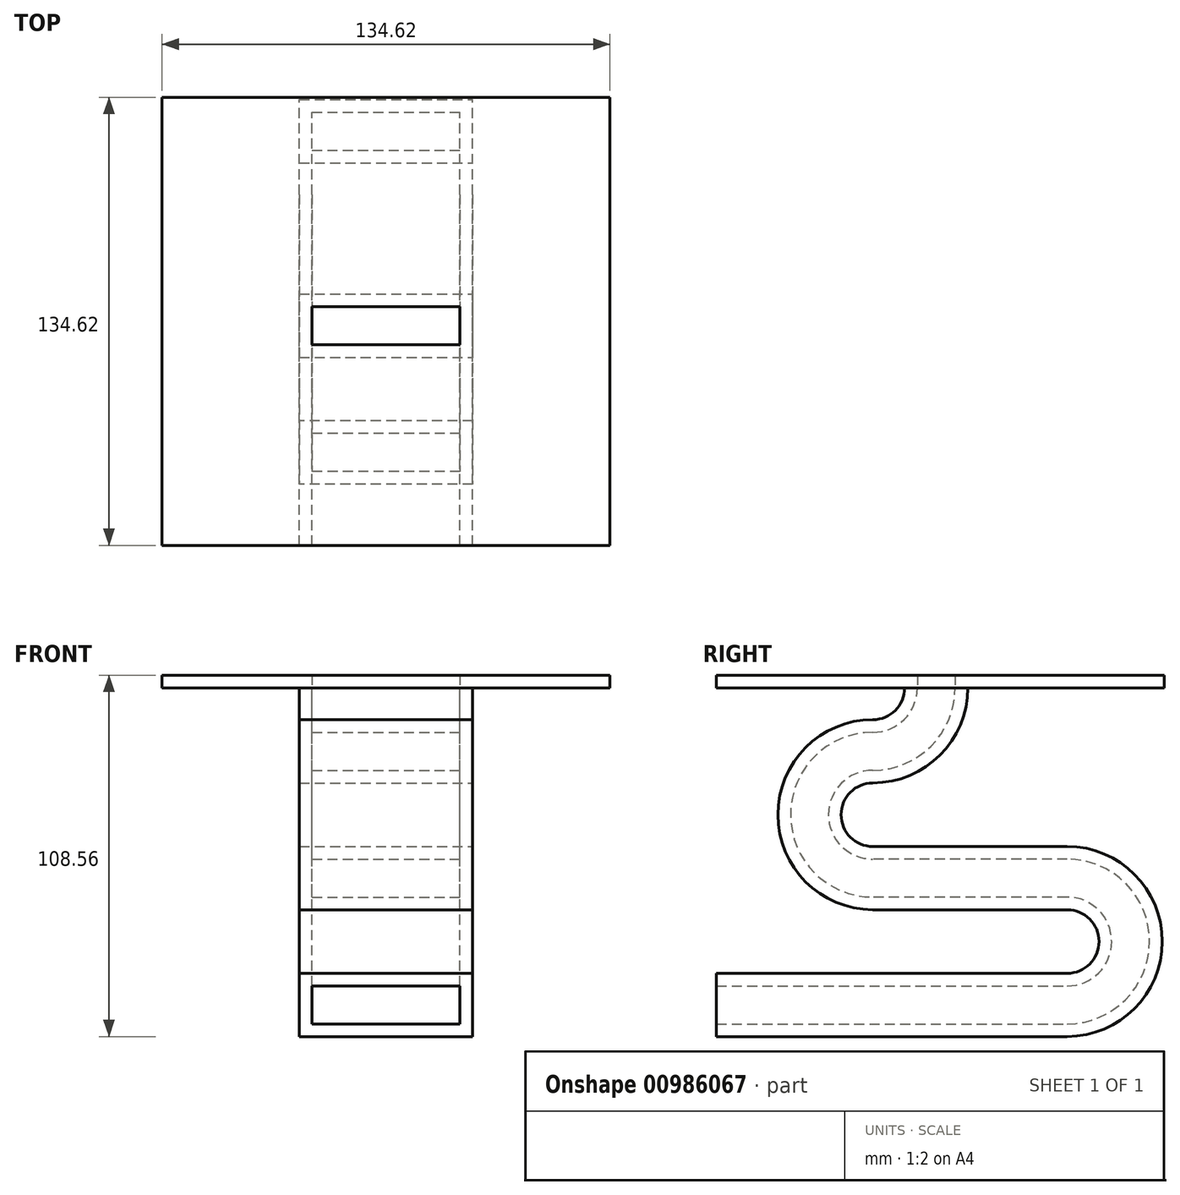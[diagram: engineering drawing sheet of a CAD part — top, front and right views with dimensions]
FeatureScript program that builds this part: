
annotation { "Feature Type Name" : "Feature", "Feature Type Description" : "" }
export const myFeature = defineFeature(function(context is Context, id is Id, definition is map)
    precondition{}
    {
        {
            var Q0;
            Q0=qCreatedBy(makeId("Front.planeOp"),FACE);
            var sketch = newSketch(context, id + "F0", { "sketchPlane" : qUnion([Q0])});
            skLineSegment(sketch, "E0.bottom", {"start": v(-22.23, 0) * mm, "end": v(22.23, 0) * mm});
            skLineSegment(sketch, "E0.top", {"start": v(-22.23, 11.4) * mm, "end": v(22.23, 11.4) * mm});
            skLineSegment(sketch, "E0.left", {"start": v(-22.23, 0) * mm, "end": v(-22.23, 11.4) * mm});
            skLineSegment(sketch, "E0.right", {"start": v(22.23, 0) * mm, "end": v(22.23, 11.4) * mm});
            skLineSegment(sketch, "E1.bottom", {"start": v(-26.04, 15.2) * mm, "end": v(26.04, 15.2) * mm});
            skLineSegment(sketch, "E1.top", {"start": v(-26.04, -3.8) * mm, "end": v(26.04, -3.81) * mm});
            skLineSegment(sketch, "E1.left", {"start": v(-26.04, 15.2) * mm, "end": v(-26.04, -3.8) * mm});
            skLineSegment(sketch, "E1.right", {"start": v(26.04, 15.2) * mm, "end": v(26.04, -3.8) * mm});
            skSolve(sketch);
        }
        {
            var Q0;
            Q0=qCreatedBy(makeId("Right.planeOp"),FACE);
            var sketch = newSketch(context, id + "F1", { "sketchPlane" : qUnion([Q0])});
            skLineSegment(sketch, "E2", {"start": v(0, 0) * mm, "end": v(0, 5.7) * mm});
            skLineSegment(sketch, "E3", {"start": v(0, 5.7) * mm, "end": v(105.41, 5.7) * mm});
            skPoint(sketch, "E4", {"position": v(105.41, 24.75) * mm});
            skArc(sketch, "E5", {"start": v(105.41, 5.7) * mm, "mid": v(124.46, 24.75) * mm, "end": v(105.4, 43.8) * mm});
            skLineSegment(sketch, "E6", {"start": v(105.4, 43.8) * mm, "end": v(47, 43.8) * mm});
            skPoint(sketch, "E7", {"position": v(47, 62.85) * mm});
            skPoint(sketch, "E8", {"position": v(124.46, 24.75) * mm});
            skPoint(sketch, "E9", {"position": v(83.13, 100.95) * mm});
            skArc(sketch, "E10", {"start": v(47, 43.8) * mm, "mid": v(27.94, 62.85) * mm, "end": v(47, 81.9) * mm});
            skPoint(sketch, "E11", {"position": v(47, 100.95) * mm});
            skArc(sketch, "E12", {"start": v(47, 81.9) * mm, "mid": v(60.46, 87.48) * mm, "end": v(66.04, 100.95) * mm});
            skSolve(sketch);
        }
        {
            var Q0;
            Q0=makeQuery(id+"F0.imprint","IMPRINT",FACE,{"disambiguationData":[TD([[makeQuery(id+"F0.imprint","IMPRINT",EDGE,{"derivedFrom":sQuery(id+"F0.wireOp",EDGE,"E0.bottom")}),-1.0]])]});
            var Q1;
            Q1=sQuery(id+"F1.wireOp",EDGE,"E3");
            var Q2;
            Q2=sQuery(id+"F1.wireOp",EDGE,"E5");
            var Q3;
            Q3=sQuery(id+"F1.wireOp",EDGE,"E6");
            var Q4;
            Q4=sQuery(id+"F1.wireOp",EDGE,"E10");
            var Q5;
            Q5=sQuery(id+"F1.wireOp",EDGE,"E12");
            sweep(context, id + "F2", {"profiles" : qUnion([Q0]), "path" : qUnion([Q1, Q2, Q3, Q4, Q5])});
        }
        {
            var Q0;
            Q0=makeQuery(id+"F2.opSweep","SWEPT_FACE",FACE,{"disambiguationData":[OSD([sQuery(id+"F0.wireOp",EDGE,"E1.top"),sQuery(id+"F1.wireOp",EDGE,"E3")])]});
            cPlane(context, id + "F3", {"entities" : qUnion([Q0]), "cplaneType" : CPlaneType.OFFSET, "offset" : 104.75 * mm, "oppositeDirection" : true, "width" : 152.4 * mm, "height" : 152.4 * mm});
        }
        {
            var Q0;
            Q0=makeQuery(id+"F2.opSweep","CAP_FACE",FACE,{"disambiguationData":[OSD([sQuery(id+"F0.wireOp",EDGE,"E0.bottom"),sQuery(id+"F0.wireOp",EDGE,"E0.top"),sQuery(id+"F0.wireOp",EDGE,"E0.left"),sQuery(id+"F0.wireOp",EDGE,"E0.right"),sQuery(id+"F0.wireOp",EDGE,"E1.bottom"),sQuery(id+"F0.wireOp",EDGE,"E1.top"),sQuery(id+"F0.wireOp",EDGE,"E1.left"),sQuery(id+"F0.wireOp",EDGE,"E1.right"),sQuery(id+"F1.wireOp",VERTEX,"E12.end")])],"isStart":false});
            var sketch = newSketch(context, id + "F4", { "sketchPlane" : qUnion([Q0])});
            skLineSegment(sketch, "E13.bottom", {"start": v(-22.23, 71.74) * mm, "end": v(22.23, 71.74) * mm});
            skLineSegment(sketch, "E13.top", {"start": v(-22.23, 60.34) * mm, "end": v(22.23, 60.34) * mm});
            skLineSegment(sketch, "E13.left", {"start": v(-22.23, 71.74) * mm, "end": v(-22.23, 60.34) * mm});
            skLineSegment(sketch, "E13.right", {"start": v(22.23, 71.74) * mm, "end": v(22.23, 60.34) * mm});
            skSolve(sketch);
        }
        {
            var Q0;
            Q0=qCreatedBy(id+"F3.planeOp",FACE);
            var sketch = newSketch(context, id + "F5", { "sketchPlane" : qUnion([Q0])});
            skLineSegment(sketch, "E14.bottom", {"start": v(-67.3, 0) * mm, "end": v(67.3, 0) * mm});
            skLineSegment(sketch, "E14.top", {"start": v(-67.3, -134.62) * mm, "end": v(67.3, -134.62) * mm});
            skLineSegment(sketch, "E14.left", {"start": v(-67.3, 0) * mm, "end": v(-67.3, -134.62) * mm});
            skLineSegment(sketch, "E14.right", {"start": v(67.31, 0) * mm, "end": v(67.31, -134.62) * mm});
            skSolve(sketch);
        }
        {
            var Q0;
            Q0=makeQuery(id+"F5.imprint","IMPRINT",FACE,{"disambiguationData":[TD([[makeQuery(id+"F5.imprint","IMPRINT",EDGE,{"derivedFrom":sQuery(id+"F5.wireOp",EDGE,"E14.bottom")}),-1.0]])]});
            extrude(context, id + "F6", {"entities" : qUnion([Q0]), "operationType" : NewBodyOperationType.ADD, "oppositeDirection" : true, "depth" : 3.8 * mm, "offsetDistance" : 25.4 * mm});
        }
        {
            var Q0;
            Q0 = qSketchRegion(id + "F4", true);
            extrude(context, id + "F7", {"entities" : qUnion([Q0]), "operationType" : NewBodyOperationType.REMOVE, "endBound" : BoundingType.UP_TO_NEXT, "depth" : 25.4 * mm, "offsetDistance" : 25.4 * mm});
        }
    });
